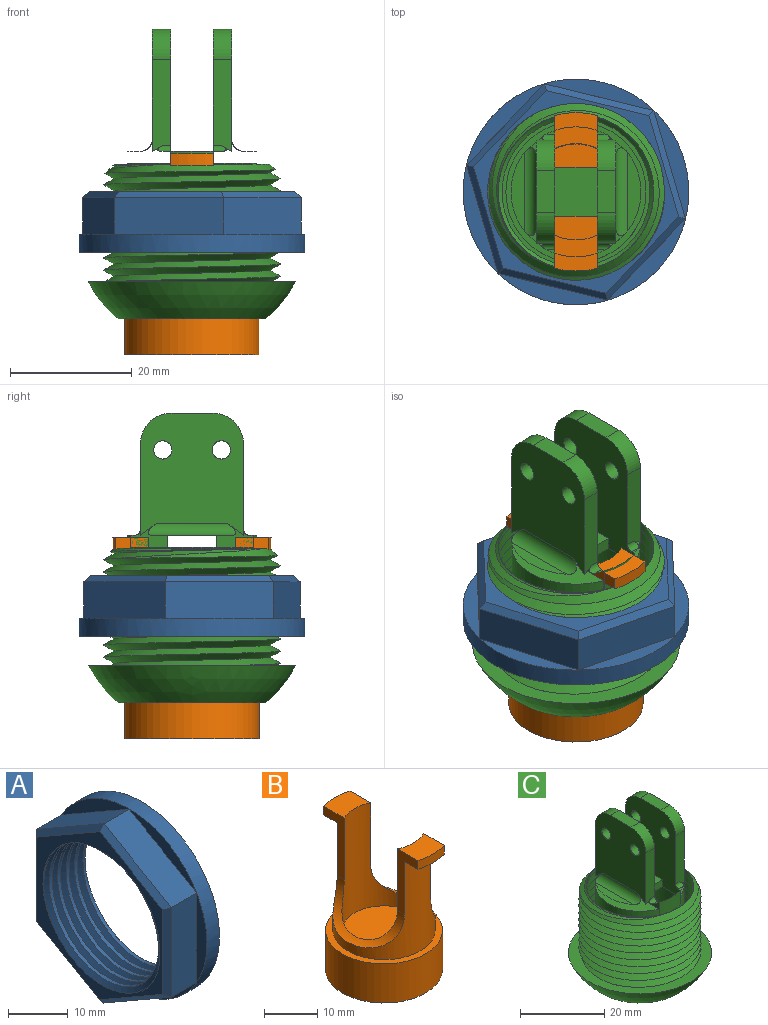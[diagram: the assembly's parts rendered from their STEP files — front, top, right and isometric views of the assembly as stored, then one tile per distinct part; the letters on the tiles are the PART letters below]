
ASSEMBLY  parts=3 mates=2
PART A: 19 faces, bbox 12.4x37.7x37.7 mm
  f0: plane 16.02x9.21mm, normal (0,0.5,0.87), area 110.9mm2, adj f1,f5,f13,f17
  f1: plane 15.98x9.27mm, normal (0,-0.5,0.87), area 110.9mm2, adj f0,f2,f14,f17
  f2: plane 18.48x6mm, normal (0,-1,0), area 110.9mm2, adj f1,f3,f12,f17
  f3: plane 16.02x9.21mm, normal (0,-0.5,-0.87), area 110.9mm2, adj f2,f4,f10,f17
  f4: plane 15.98x9.27mm, normal (0,0.5,-0.87), area 110.9mm2, adj f3,f5,f9,f17
  f5: plane 18.48x6mm, normal (0,1,0), area 110.9mm2, adj f0,f4,f11,f17
  f6: cylinder r=13.48mm len=26.96mm, axis (1,0,0), area 298mm2, adj f7,f8,f15,f16
  f7: plane 35.35x30.75mm, normal (-1,0,0), area 177mm2, adj f6,f9,f10,f11,f12,f13,f14,f15
  f8: plane 37.71x37.71mm, normal (1,0,0), area 472.8mm2, adj f6,f15,f16,f18
  f9: plane 15.98x9.84mm, normal (-0.71,0.35,-0.61), area 25.3mm2, adj f4,f7,f10,f11
  f10: plane 16.02x9.79mm, normal (-0.71,-0.35,-0.61), area 25.3mm2, adj f3,f7,f9,f12
  f11: plane 18.48x1.04mm, normal (-0.71,0.71,0), area 25.3mm2, adj f5,f7,f9,f13
  f12: plane 18.48x1.04mm, normal (-0.71,-0.71,0), area 25.3mm2, adj f2,f7,f10,f14
  f13: plane 16.02x9.79mm, normal (-0.71,0.35,0.61), area 25.3mm2, adj f0,f7,f11,f14
  f14: plane 15.98x9.84mm, normal (-0.71,-0.35,0.61), area 25.3mm2, adj f1,f7,f12,f13
  f15: bspline ~33.72x29.21mm, area 572.9mm2, adj f6,f7,f8,f16
  f16: bspline ~33.72x29.21mm, area 572.6mm2, adj f6,f7,f8,f15
  f17: plane 37x37mm, normal (-1,0,0), area 188.4mm2, adj f0,f1,f2,f3,f4,f5,f18
  f18: cylinder r=18.5mm len=37mm, axis (1,0,0), area 348.7mm2, adj f8,f17
PART B: 19 faces, bbox 22x26x33 mm
  f0: cylinder r=7.9mm len=24mm, axis (0,0,-1), area 487.7mm2, adj f1,f2,f11,f13,f14,f15,f16,f17
  f1: plane 7x5.92mm, normal (0,0,1), area 36.5mm2, adj f0,f3,f13,f16
  f2: plane 7x5.92mm, normal (0,0,1), area 36.5mm2, adj f0,f4,f15,f18
  f3: cylinder r=13mm len=7mm, axis (0,0,-1), area 14.2mm2, adj f1,f6,f13,f16
  f4: cylinder r=13mm len=7mm, axis (0,0,-1), area 14.2mm2, adj f2,f5,f15,f18
  f5: plane 7x4.06mm, normal (0,0,-1), area 24.2mm2, adj f4,f7,f15,f18
  f6: plane 7x4.06mm, normal (0,0,-1), area 24.2mm2, adj f3,f7,f13,f16
  f7: cylinder r=9.6mm len=22mm, axis (0,0,-1), area 467.6mm2, adj f5,f6,f12,f13,f14,f15,f16,f17
  f8: cylinder r=11mm len=22mm, axis (0,0,-1), area 622mm2, adj f9,f12
  f9: plane 22x22mm, normal (0,0,-1), area 33.8mm2, adj f8,f10
  f10: sphere r=19.88mm, area 374.6mm2, adj f9
  f11: plane 15.8x15.8mm, normal (0,0,1), area 196.1mm2, adj f0
  f12: plane 22x22mm, normal (0,0,1), area 90.6mm2, adj f7,f8
  f13: plane 14.23x5.44mm, normal (-1,0,0), area 33.6mm2, adj f0,f1,f3,f6,f7,f14
  f14: cylinder r=8mm len=17.88mm, axis (0,-1,0), area 53.5mm2, adj f0,f7,f13,f15
  f15: plane 14.23x5.44mm, normal (-1,0,0), area 33.6mm2, adj f0,f2,f4,f5,f7,f14
  f16: plane 14.23x5.44mm, normal (1,0,0), area 33.6mm2, adj f0,f1,f3,f6,f7,f17
  f17: cylinder r=8mm len=17.88mm, axis (0,-1,0), area 53.5mm2, adj f0,f7,f16,f18
  f18: plane 14.23x5.44mm, normal (1,0,0), area 33.6mm2, adj f0,f2,f4,f5,f7,f17
PART C: 50 faces, bbox 35.6x35.6x49.1 mm
  f0: cylinder r=11.5mm len=23mm, axis (0,0,-1), area 614.2mm2, adj f12,f45
  f1: sphere r=19.04mm, area 729.8mm2, adj f13,f45
  f2: plane 1.44x0.62mm, normal (0,0,1), area 0.5mm2, adj f14,f19,f42
  f3: plane 12.85x2.16mm, normal (0,0,1), area 18.9mm2, adj f14,f39
  f4: plane 8x7mm, normal (0,0,1), area 56mm2, adj f15,f18,f19,f21
  f5: plane 1.44x0.62mm, normal (0,0,1), area 0.5mm2, adj f14,f19,f41
  f6: plane 1.44x0.62mm, normal (0,0,1), area 0.5mm2, adj f14,f21,f44
  f7: plane 12.85x2.16mm, normal (0,0,1), area 18.9mm2, adj f14,f40
  f8: cylinder r=10.5mm len=21mm, axis (0,0,-1), area 1093mm2, adj f9,f12,f17,f19,f21,f22
  f9: plane 21x19.8mm, normal (0,0,-1), area 258.1mm2, adj f8,f15,f18,f19,f21
  f10: plane 1.44x0.62mm, normal (0,0,1), area 0.5mm2, adj f14,f21,f43
  f11: cylinder r=12.75mm len=25.5mm, axis (0,0,-1), area 1546.6mm2, adj f13,f14
  f12: plane 23x23mm, normal (0,0,-1), area 69.1mm2, adj f0,f8
  f13: plane 35.6x35.6mm, normal (0,0,1), area 325.2mm2, adj f1,f11,f46,f47,f48
  f14: cone r=4.01mm half-angle=45deg, axis (0,0,-1), area 225.3mm2, adj f2,f3,f5,f6,f7,f10,f11,f16
  f15: plane 7x2mm, normal (0,-1,0), area 14mm2, adj f4,f9,f19,f21
  f16: cylinder r=10.66mm len=7mm, axis (0,0,1), area 28.5mm2, adj f14,f17,f19,f21
  f17: plane 7x0.76mm, normal (0,0,1), area 1.1mm2, adj f8,f16,f19,f21
  f18: plane 7x2mm, normal (0,1,0), area 14mm2, adj f4,f9,f19,f21
  f19: plane 24x20.13mm, normal (-1,0,0), area 338.2mm2, adj f2,f4,f5,f8,f9,f15,f16,f17
  f20: cylinder r=10.66mm len=7mm, axis (0,0,1), area 28.5mm2, adj f14,f19,f21,f22
  f21: plane 24x20.13mm, normal (1,0,0), area 338.2mm2, adj f4,f6,f8,f9,f10,f15,f16,f17
  f22: plane 7x0.76mm, normal (0,0,1), area 1.1mm2, adj f8,f19,f20,f21
  f23: plane 15.11x3.11mm, normal (0,1,0), area 42.9mm2, adj f14,f21,f24,f37,f43
  f24: plane 20.24x17.13mm, normal (-1,0,0), area 284.4mm2, adj f14,f23,f25,f26,f33,f34,f37,f38
  f25: plane 15.11x3.11mm, normal (0,-1,0), area 42.9mm2, adj f14,f21,f24,f38,f44
  f26: plane 6.89x3mm, normal (0,0,1), area 20.7mm2, adj f21,f24,f37,f38
  f27: plane 15.11x3.11mm, normal (0,-1,0), area 42.9mm2, adj f14,f19,f28,f35,f41
  f28: plane 20.24x17.13mm, normal (1,0,0), area 284.4mm2, adj f14,f27,f29,f30,f31,f32,f35,f36
  f29: plane 15.11x3.11mm, normal (0,1,0), area 42.9mm2, adj f14,f19,f28,f36,f42
  f30: plane 6.89x3mm, normal (0,0,1), area 20.7mm2, adj f19,f28,f35,f36
  f31: cylinder r=1.5mm len=3mm, axis (-1,0,0), area 28.3mm2, adj f19,f28
  f32: cylinder r=1.5mm len=3mm, axis (-1,0,0), area 28.3mm2, adj f19,f28
  f33: cylinder r=1.5mm len=3mm, axis (-1,0,0), area 28.3mm2, adj f21,f24
  f34: cylinder r=1.5mm len=3mm, axis (-1,0,0), area 28.3mm2, adj f21,f24
  f35: cylinder r=5mm len=5mm, axis (-1,0,0), area 23.6mm2, adj f19,f27,f28,f30
  f36: cylinder r=5mm len=5mm, axis (1,0,0), area 23.6mm2, adj f19,f28,f29,f30
  f37: cylinder r=5mm len=5mm, axis (1,0,0), area 23.6mm2, adj f21,f23,f24,f26
  f38: cylinder r=5mm len=5mm, axis (-1,0,0), area 23.6mm2, adj f21,f24,f25,f26
  f39: cylinder r=2mm len=12.85mm, axis (0,1,0), area 38.1mm2, adj f3,f14,f28
  f40: cylinder r=2mm len=12.85mm, axis (0,-1,0), area 38.1mm2, adj f7,f14,f24
  f41: cylinder r=1mm len=2.08mm, axis (1,0,0), area 2.9mm2, adj f5,f14,f19,f27
  f42: cylinder r=1mm len=2.08mm, axis (-1,0,0), area 2.9mm2, adj f2,f14,f19,f29
  f43: cylinder r=1mm len=2.08mm, axis (-1,0,0), area 2.9mm2, adj f10,f14,f21,f23
  f44: cylinder r=1mm len=2.08mm, axis (1,0,0), area 2.9mm2, adj f6,f14,f21,f25
  f45: plane 24.26x24.26mm, normal (0,0,-1), area 46.9mm2, adj f0,f1
  f46: bspline ~33.49x29mm, area 1571.9mm2, adj f13,f47,f48,f49
  f47: cylinder r=12.78mm len=25.55mm, axis (0,0,-1), area 1523.6mm2, adj f13,f46,f48,f49
  f48: bspline ~33.49x29mm, area 1567.1mm2, adj f13,f46,f47,f49
  f49: cone r=4.01mm half-angle=45deg, axis (0,0,-1), area 101.9mm2, adj f46,f47,f48
PLACE A rot(axis=(-0.63,0.47,0.63),129.9deg) t=(-5.89,5.57,-7.75)mm
PLACE B t=(-5.89,5.57,-15.51)mm
PLACE C t=(-5.89,5.57,-12.54)mm fixed
MATE slider B.f0 <-> C.f0  axis (0,0,-1) through (-5.89,5.57,-15.51)mm
MATE cylindrical A.f18 <-> C.f0  axis (0,0,-1) through (-5.89,5.57,-6.25)mm
